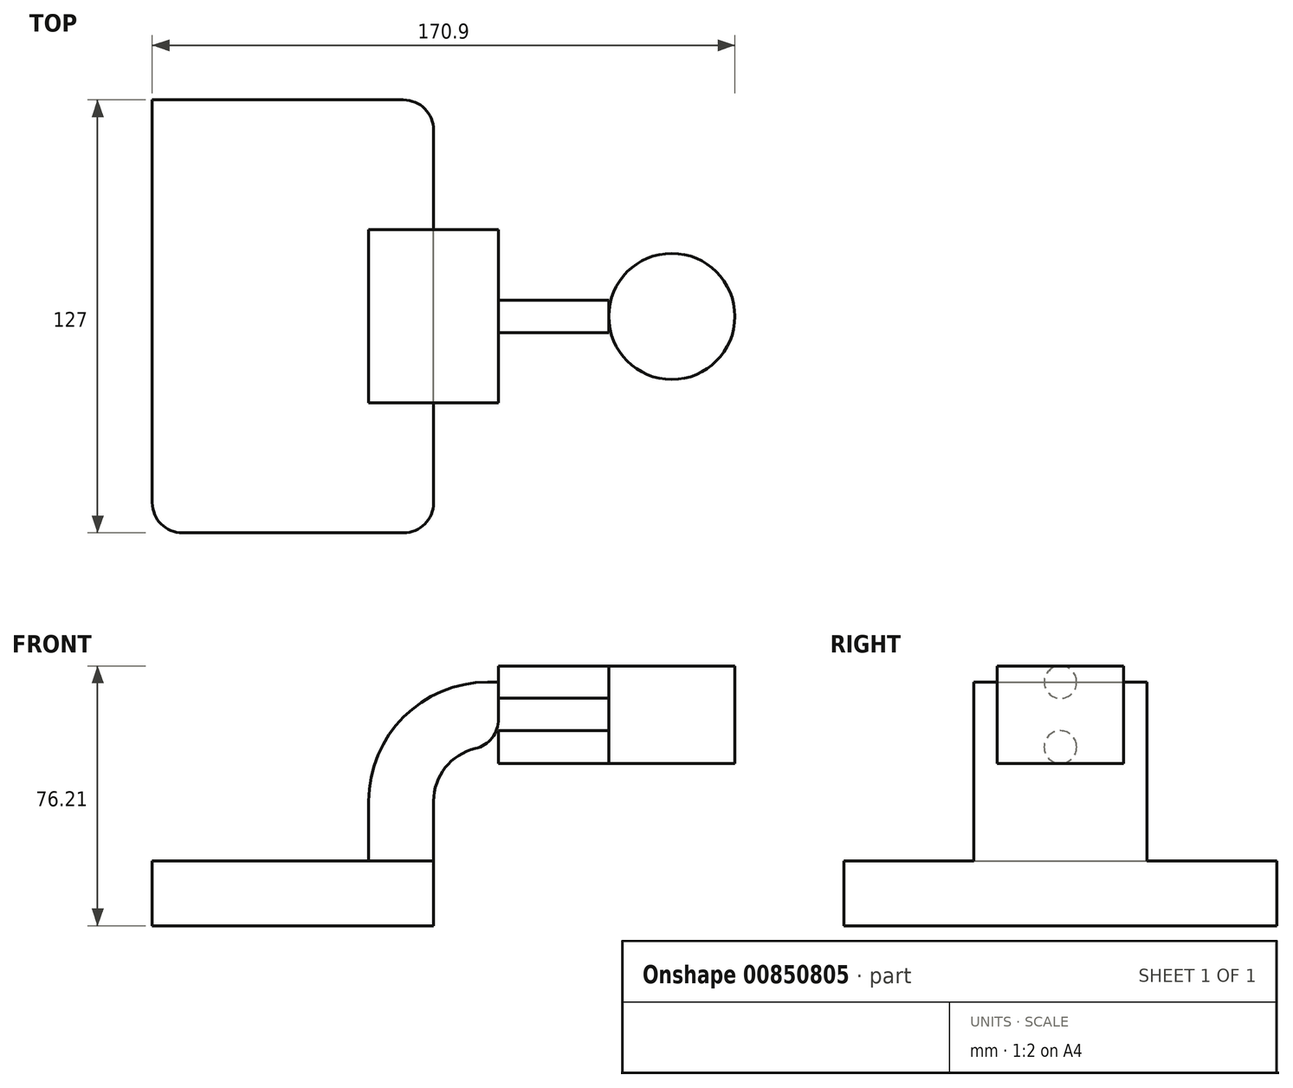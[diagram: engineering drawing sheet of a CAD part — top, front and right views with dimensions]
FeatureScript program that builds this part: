
annotation { "Feature Type Name" : "Feature", "Feature Type Description" : "" }
export const myFeature = defineFeature(function(context is Context, id is Id, definition is map)
    precondition{}
    {
        {
            var Q0;
            Q0=qCreatedBy(makeId("Front.planeOp"),FACE);
            var sketch = newSketch(context, id + "F0", { "sketchPlane" : qUnion([Q0])});
            skLineSegment(sketch, "E0.bottom", {"start": v(41.27, 9.53) * mm, "end": v(-41.27, 9.53) * mm});
            skLineSegment(sketch, "E0.top", {"start": v(41.28, -9.52) * mm, "end": v(-41.27, -9.52) * mm});
            skLineSegment(sketch, "E0.left", {"start": v(41.28, 9.53) * mm, "end": v(41.28, -9.52) * mm});
            skLineSegment(sketch, "E0.right", {"start": v(-41.27, 9.53) * mm, "end": v(-41.27, -9.52) * mm});
            skPoint(sketch, "E0.middle", {"position": v(0, 0) * mm});
            skLineSegment(sketch, "E1.bottom", {"start": v(111.13, 38.1) * mm, "end": v(60.33, 38.1) * mm});
            skLineSegment(sketch, "E1.top", {"start": v(111.13, 66.68) * mm, "end": v(60.33, 66.68) * mm});
            skLineSegment(sketch, "E1.left", {"start": v(111.13, 38.1) * mm, "end": v(111.13, 66.68) * mm});
            skLineSegment(sketch, "E1.right", {"start": v(60.33, 38.1) * mm, "end": v(60.33, 66.68) * mm});
            skPoint(sketch, "E1.middle", {"position": v(85.73, 52.39) * mm});
            skLineSegment(sketch, "E2", {"start": v(41.27, 9.53) * mm, "end": v(41.27, 27) * mm});
            skArc(sketch, "E3", {"start": v(41.27, 27) * mm, "mid": v(45.92, 38.23) * mm, "end": v(57.15, 42.88) * mm});
            skLineSegment(sketch, "E4", {"start": v(57.15, 42.88) * mm, "end": v(92.63, 42.88) * mm});
            skLineSegment(sketch, "E5.0", {"start": v(57.15, 61.93) * mm, "end": v(92.63, 61.93) * mm});
            skArc(sketch, "E5.1", {"start": v(22.22, 27) * mm, "mid": v(32.45, 51.7) * mm, "end": v(57.15, 61.93) * mm});
            skLineSegment(sketch, "E5.2", {"start": v(22.22, 9.53) * mm, "end": v(22.22, 27) * mm});
            skFitSpline(sketch, "E6", {"points": [v(-41.27, 9.52) * mm, v(57.15, 61.93) * mm], "startDerivative": vector(135.86, 81.88) * mm, "endDerivative": vector(150.45, -16.76) * mm});
            skLineSegment(sketch, "E7", {"start": v(92.63, 38.1) * mm, "end": v(92.63, 66.68) * mm});
            skSolve(sketch);
        }
        {
            var Q0;
            Q0=makeQuery(id+"F0.imprint","IMPRINT",FACE,{"disambiguationData":[TD([[makeQuery(id+"F0.imprint","IMPRINT",EDGE,{"derivedFrom":sQuery(id+"F0.wireOp",EDGE,"E0.top")}),-1.0]])]});
            extrude(context, id + "F1", {"entities" : qUnion([Q0]), "endBound" : BoundingType.SYMMETRIC, "depth" : 127 * mm, "offsetDistance" : 25.4 * mm});
        }
        {
            var Q0;
            {var subQ1=sQuery(id+"F0.wireOp",EDGE,"E2");Q0=makeQuery(id+"F0.imprint","IMPRINT",FACE,{"disambiguationData":[TD([[makeQuery(id+"F0.imprint","IMPRINT",EDGE,{"derivedFrom":subQ1}),1.0]])]});}
            extrude(context, id + "F2", {"entities" : qUnion([Q0]), "operationType" : NewBodyOperationType.ADD, "endBound" : BoundingType.SYMMETRIC, "depth" : 50.8 * mm, "offsetDistance" : 25.4 * mm});
        }
        {
            var Q0;
            Q0=makeQuery(id+"F0.imprint","IMPRINT",FACE,{"disambiguationData":[TD([[makeQuery(id+"F0.imprint","IMPRINT",EDGE,{"derivedFrom":sQuery(id+"F0.wireOp",EDGE,"E5.1")}),1.0]])]});
            extrude(context, id + "F3", {"entities" : qUnion([Q0]), "operationType" : NewBodyOperationType.ADD, "depth" : 15.88 * mm, "offsetDistance" : 25.4 * mm});
        }
        {
            var Q0;
            {var subQ0=sQuery(id+"F0.wireOp",EDGE,"E1.left");Q0=makeQuery(id+"F0.imprint","IMPRINT",FACE,{"disambiguationData":[TD([[makeQuery(id+"F0.imprint","IMPRINT",EDGE,{"derivedFrom":subQ0}),1.0]])]});}
            var Q1;
            Q1=sQuery(id+"F0.wireOp",EDGE,"E1.left");
            revolve(context, id + "F4", {"surfaceOperationType" : NewSurfaceOperationType.NEW, "entities" : qUnion([Q0]), "axis" : qUnion([Q1]), "revolveType" : RevolveType.FULL});
        }
        {
            var Q0;
            Q0=makeQuery(id+"F1.opExtrude","CAP_EDGE",EDGE,{"disambiguationData":[OSD([sQuery(id+"F0.wireOp",EDGE,"E0.left")])],"isStart":false});
            var Q1;
            Q1=makeQuery(id+"F1.opExtrude","CAP_EDGE",EDGE,{"disambiguationData":[OSD([sQuery(id+"F0.wireOp",EDGE,"E0.right")])],"isStart":false});
            var Q2;
            Q2=makeQuery(id+"F1.opExtrude","CAP_EDGE",EDGE,{"disambiguationData":[OSD([sQuery(id+"F0.wireOp",EDGE,"E0.left")])],"isStart":true});
            var Q3;
            Q3=makeQuery(id+"F2.opExtrude","SWEPT_EDGE",EDGE,{"disambiguationData":[OSD([sQuery(id+"F0.wireOp",EDGE,"E1.right"),sQuery(id+"F0.wireOp",EDGE,"E4")])]});
            fillet(context, id + "F5", {"entities" : qUnion([Q0, Q1, Q2, Q3]), "radius" : 8.9 * mm, "tangentPropagation" : true, "allowEdgeOverflow" : false});
        }
        {
            var Q0;
            {var subQ0=sQuery(id+"F0.wireOp",EDGE,"E1.right");var subQ1=sQuery(id+"F0.wireOp",EDGE,"E1.bottom");var subQ2=makeQuery(id+"F0.imprint","INTERSECT",VERTEX,{"derivedFrom":[subQ1,subQ0]});Q0=makeQuery(id+"F0.imprint","IMPRINT",FACE,{"disambiguationData":[TD([[makeQuery(id+"F0.imprint","IMPRINT",EDGE,{"disambiguationData":[TD([[subQ2,1.0]])],"derivedFrom":subQ1}),-1.0]])]});}
            var Q1;
            Q1=sQuery(id+"F0.wireOp",EDGE,"E4");
            revolve(context, id + "F6", {"operationType" : NewBodyOperationType.ADD, "surfaceOperationType" : NewSurfaceOperationType.NEW, "entities" : qUnion([Q0]), "axis" : qUnion([Q1]), "revolveType" : RevolveType.FULL});
        }
        {
            var Q0;
            {var subQ0=sQuery(id+"F0.wireOp",EDGE,"E1.right");var subQ1=sQuery(id+"F0.wireOp",EDGE,"E1.top");var subQ2=makeQuery(id+"F0.imprint","INTERSECT",VERTEX,{"derivedFrom":[subQ1,subQ0]});Q0=makeQuery(id+"F0.imprint","IMPRINT",FACE,{"disambiguationData":[TD([[makeQuery(id+"F0.imprint","IMPRINT",EDGE,{"disambiguationData":[TD([[subQ2,1.0]])],"derivedFrom":subQ1}),1.0]])]});}
            var Q1;
            Q1=sQuery(id+"F0.wireOp",EDGE,"E5.0");
            revolve(context, id + "F7", {"surfaceOperationType" : NewSurfaceOperationType.NEW, "entities" : qUnion([Q0]), "axis" : qUnion([Q1]), "revolveType" : RevolveType.FULL});
        }
    });
